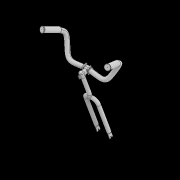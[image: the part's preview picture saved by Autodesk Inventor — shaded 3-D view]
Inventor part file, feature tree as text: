
AUTODESK INVENTOR PART (.ipt)
format: ipt  version: 2021 (Build 250183000, 183)  size: 4,962,816 bytes
history: native  units: in
note: dims shown in document units (in); Inventor stores cm internally (conversion verified against a paired STEP export)
features: plane x33, sketch x30, extrude x13, other x8, projected_geometry x7, loft x6, mirror x4, fillet x3, hole x2, split x2, sweep x1, move_body x1, revolve x1
ambient origin geometry x8: Origin, YZ Plane, XZ Plane, XY Plane, X Axis, Y Axis, Z Axis, Center Point
bodies: Solid3 (feature_tree), Solid4 (feature_tree), Solid6 (feature_tree), Solid8 (feature_tree), Solid12 (feature_tree), Solid14 (feature_tree), Solid15 (feature_tree), Solid16 (feature_tree), Solid10 (feature_tree), Solid11 (feature_tree)
feature tree (111):
  sketch  "3D Sketch1"
  plane  "Work Plane6"
  sweep  "Sweep3"
  plane  "Work Plane4"
  plane  "Work Plane5"
  sketch  "Sketch14"  dims[d24=1.66in d25=0.0in d26=0.0in]
  sketch  "Sketch15"  dims[d28=2.0472in d29=0.0in d30=90.0deg d31=0.0in d32=90.0deg]
  loft  "Loft1"
  loft  "Loft2"
  plane  "Work Plane7"
  sketch  "Sketch16"  dims[d33=0.0in d34=90.0deg d35=0.0in d36=90.0deg d37=0.0in d42=180.0deg]
  plane  "Work Plane8"
  extrude  "Extrusion2"  TaperAngle=180.0deg  [1 undecoded]
  extrude  "Extrusion3"  Depth=1.378in TaperAngle=0.0deg
  plane  "Work Plane9"
  extrude  "Extrusion4"  Depth=1.7225in TaperAngle=0.0deg
  extrude  "Extrusion5"  Depth=1.1024in
  plane  "Work Plane22"
  sketch  "Sketch33"  dims[d119=0.1181in]
  plane  "Work Plane23"
  extrude  "Extrusion10"  Depth=0.1969in
  plane  "Work Plane19"
  plane  "Work Plane20"
  extrude  "Extrusion11"  Depth=0.4331in
  fillet  "Fillet1"  Radius=0.0197in
  plane  "Work Plane24"
  plane  "Work Plane25"
  hole  "Hole1"  [1 undecoded]
  mirror  "Mirror5"
  other  "Work Axis4"
  mirror  "Mirror3"
  plane  "Work Plane34"
  extrude  "Extrusion13"  Depth=0.3937in TaperAngle=0.0deg
  fillet  "Fillet2"  Radius=0.0984in
  plane  "Work Plane35"
  hole  "Hole2"  [1 undecoded]
  plane  "Work Plane36"
  sketch  "Sketch44"  dims[d188=0.1969in]
  split  "Split2"
  plane  "Work Plane26"
  split  "Split1"
  sketch  "Sketch21"  dims[d73=0.3937in d74=0.0in d79=0.4331in d80=0.0197in]
  other  "Work Axis1"
  move_body  "Move Body2"
  plane  "Work Plane10"
  plane  "Work Plane11"
  plane  "Work Plane12"
  sketch  "Sketch24"  dims[d94=0.0in d95=90.0deg d96=0.0in d97=90.0deg d98=0.3937in d99=0.0in d105=0.0984in]
  extrude  "Extrusion6"  [1 undecoded]
  sketch  "Sketch23"  dims[d85=15.0016in d86=1.38in]
  loft  "Loft5"
  loft  "Loft8"
  plane  "Work Plane13"
  extrude  "Extrusion8"  TaperAngle=180.0deg  [1 undecoded]
  other  "Work Axis5"
  other  "Bend Part2"
  plane  "Work Plane30"
  sketch  "Sketch36"  dims[d131=90.0deg d132=180.0deg]
  loft  "Loft10"
  sketch  "Sketch38"  dims[d140=1.66in d144=90.0deg]
  plane  "Work Plane31"
  loft  "Loft12"
  plane  "Work Plane32"
  extrude  "Extrusion12"  Depth=1.38in
  mirror  "Mirror6"
  plane  "Work Plane33"
  sketch  "Sketch41"  dims[d153=90.0deg d154=0.0in d155=0.7874in]
  plane  "Work Plane37"
  revolve  "Revolution2"  [1 undecoded]
  plane  "Work Plane38"
  extrude  "Extrusion14"  Depth=0.7874in TaperAngle=0.0deg
  plane  "Work Plane39"
  extrude  "Extrusion15"  TaperAngle=0.0deg  [1 undecoded]
  fillet  "Fillet3"  Radius=1.9685in
  plane  "Work Plane40"
  extrude  "Extrusion16"  Depth=0.1969in
  mirror  "Mirror7"
  sketch  "Sketch13"  dims[d19=0.0in d21=1.378in d23=1.38in]
  sketch  "Sketch17"  dims[d43=0.3937in d44=0.0in d45=1.378in d46=0.0in]
  sketch  "Sketch18"  dims[d48=180.0deg d49=1.7225in d50=0.0in]
  sketch  "Sketch19"  dims[d53=0.8661in d54=0.0in d55=1.1024in]
  sketch  "Sketch20"  dims[d57=180.0deg d60=0.1969in]
  sketch  "Sketch25"  dims[d112=0.3937in d113=0.0in d114=0.3937in d115=0.0in]
  plane  "Work Plane18"
  sketch  "Sketch32"  dims[d116=0.1969in d117=-1.0236in]
  plane  "Work Plane21"
  sketch  "Sketch34"  dims[d121=2.0in d122=0.1575in d123=0.0787in d124=90.0deg d125=1.66in d126=0.8108in]
  plane  "Work Plane27"
  plane  "Work Plane28"
  sketch  "Sketch35"  dims[d127=0.4921in d128=0.0in]
  other  "Pattern of Solid8:2"
  plane  "Work Plane29"
  sketch  "Sketch37"  dims[d138=1.38in d139=1.66in]
  other  "Edges7"
  other  "Edges8"
  sketch  "Sketch39"  dims[d145=180.0deg d146=1.38in]
  sketch  "Sketch40"  dims[d149=1.1024in d152=1.1811in]
  sketch  "Sketch42"  dims[d173=0.0in d174=90.0deg d175=0.0in d176=90.0deg d177=0.0in d178=90.0deg d180=1.9685in]
  sketch  "Sketch43"  dims[d186=0.1969in d187=0.1969in]
  sketch  "Sketch45"  dims[d189=0.0in d190=90.0deg]
  sketch  "Sketch46"  dims[d191=0.0in d192=90.0deg]
  sketch  "Sketch47"  dims[d193=0.1575in]
  sketch  "Sketch48"  dims[d194=0.5961in d195=0.69in d196=0.0in d197=0.0in d198=0.0in d205=0.0in d206=0.9843in d208=0.7874in d210=0.1969in d211=0.3937in d212=0.0in d215=0.3369in d216=0.4921in d218=0.5629in d219=0.2362in d220=0.1181in d221=0.0in d222=0.1575in d223=0.2362in d224=0.1575in d225=0.0787in d226=90.0deg d227=1.66in d228=0.8108in d229=0.0in d236=0.0in d237=90.0deg d238=0.0in d239=90.0deg d246=0.14in d247=0.315in d248=0.83in d249=90.0deg d250=-3.937in d251=1.9685in d252=5.9055in d253=0.0in d254=0.0in d255=2.1654in d256=0.3937in d257=0.0in d258=0.0787in d259=0.0in d260=0.1575in d261=0.3937in d262=0.0in d141=0.0344in]
  other  "Pattern of Solid15:3"
  projected_geometry  "Project Cut Edges2"
  projected_geometry  "Project Cut Edges3"
  projected_geometry  "Project Cut Edges4"
  projected_geometry  "Project Cut Edges5"
  projected_geometry  "Project Cut Edges6"
  projected_geometry  "Project Cut Edges7"
  projected_geometry  "Project Cut Edges10"
note: 7 required parameter values undecoded (feature->parameter linkage not recoverable at this tier; creation-order binding heuristic only, values carry confidence <= 0.55)